# Revit family: Скамейка парковая «Прага двухсторонняя»
name_source: partatom
category: Мебель
revit_build: Autodesk Revit 2017 (Build: 20160225_1515(x64)
units: mm (PartAtom-declared; Revit-internal decimal feet)

## family parameters
Всегда вертикально = Да
Заголовок OmniClass = General Furniture and Specialties
На основе рабочей плоскости = Нет
Номер OmniClass = 23.40.20.00
Общий = Нет
При загрузке вырезать с полостями = Нет
Точка расчета площади = Нет

## types (4) — shared parameters
ADSK_Код изделия = 10082
ADSK_Материал доски = <По категории>
ADSK_Материал опоры = <По категории>
ADSK_Материал фурнитуры = <По категории>
ADSK_Размер_Высота = 990 мм
ADSK_Размер_Ширина = 880 мм
URL = https://hobbyka.ru
Изготовитель = ООО "Хоббика"

## per-type parameters (varying)
| type | ADSK_Размер_Длина | Длина доски | С_Количество_опор_Видимость | Стоимость |
| Скамейка парковая «Прага двухсторонняя» 1.5м | 1500 мм | 1530 мм | Нет | 24800 $ |
| Скамейка парковая «Прага двухсторонняя» 1,8м | 1800 мм | 1830 мм | Нет | 27994 $ |
| Скамейка парковая «Прага двухсторонняя» 2,0м (3 опоры) | 2000 мм | 2030 мм | Да | 41127 $ |
| Скамейка парковая «Прага двухсторонняя» 3,0м | 3000 мм | 3030 мм | Да | 42885 $ |

note: column(s) folded — value = type name in every type: ADSK_Наименование
